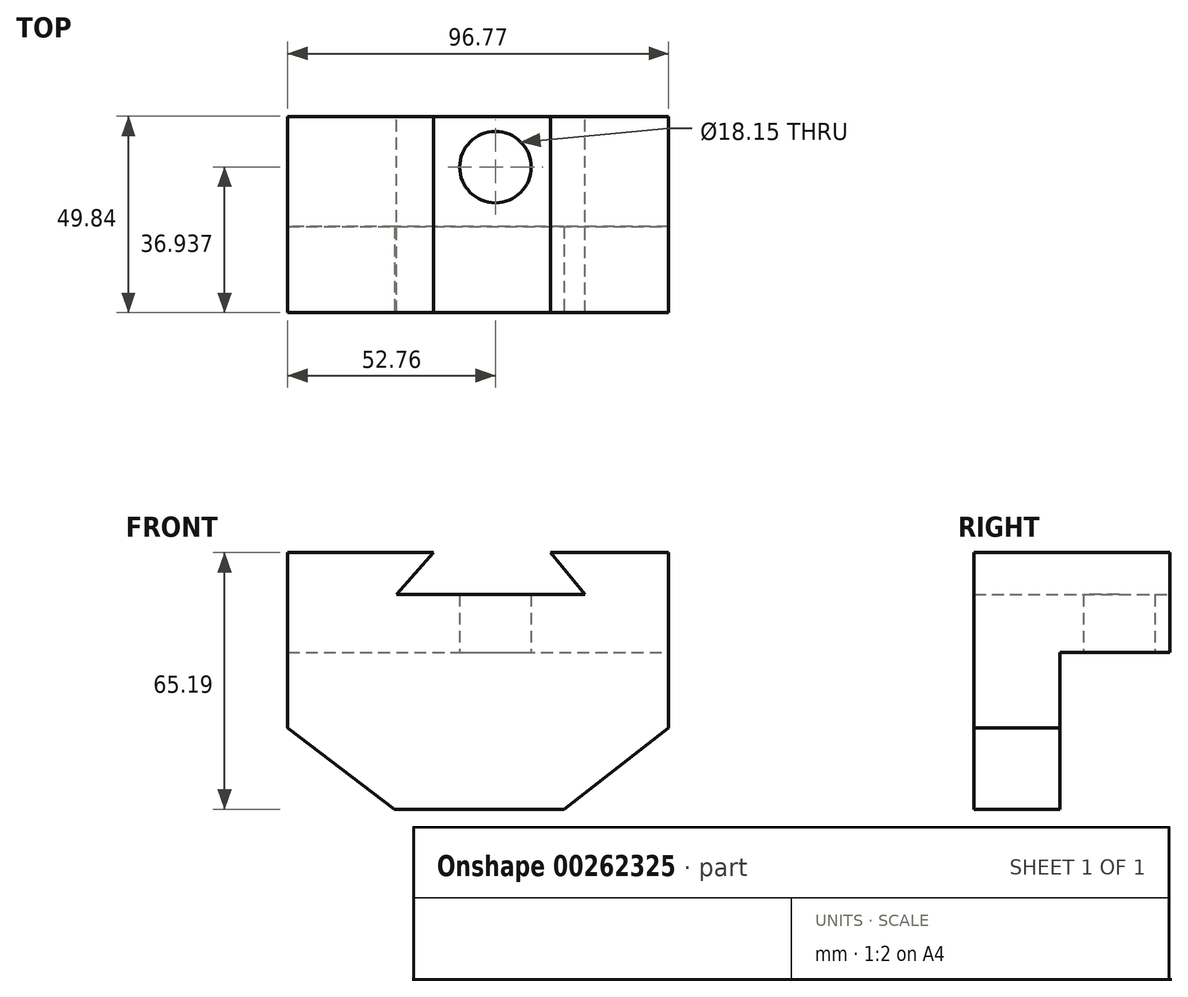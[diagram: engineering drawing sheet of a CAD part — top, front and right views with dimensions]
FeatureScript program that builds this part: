
annotation { "Feature Type Name" : "Feature", "Feature Type Description" : "" }
export const myFeature = defineFeature(function(context is Context, id is Id, definition is map)
    precondition{}
    {
        {
            var Q0;
            Q0=qCreatedBy(makeId("Top.planeOp"),FACE);
            var sketch = newSketch(context, id + "F0", { "sketchPlane" : qUnion([Q0])});
            skLineSegment(sketch, "E0.bottom", {"start": v(-52.76, 22.59) * mm, "end": v(44.01, 22.59) * mm});
            skLineSegment(sketch, "E0.top", {"start": v(-52.76, -27.25) * mm, "end": v(44.01, -27.25) * mm});
            skLineSegment(sketch, "E0.left", {"start": v(-52.76, 22.59) * mm, "end": v(-52.76, -27.25) * mm});
            skLineSegment(sketch, "E0.right", {"start": v(44.01, 22.59) * mm, "end": v(44.01, -27.25) * mm});
            skSolve(sketch);
        }
        {
            var Q0;
            Q0 = qSketchRegion(id + "F0", true);
            extrude(context, id + "F1", {"entities" : qUnion([Q0]), "depth" : 25.4 * mm});
        }
        {
            var Q0;
            Q0=makeQuery(id+"F1.opExtrude","SWEPT_FACE",FACE,{"disambiguationData":[OSD([sQuery(id+"F0.wireOp",EDGE,"E0.top")])]});
            var sketch = newSketch(context, id + "F2", { "sketchPlane" : qUnion([Q0])});
            skLineSegment(sketch, "E1.bottom", {"start": v(44.01, 25.4) * mm, "end": v(-52.76, 25.4) * mm});
            skLineSegment(sketch, "E1.top", {"start": v(44.01, -19.1) * mm, "end": v(-52.76, -19.1) * mm});
            skLineSegment(sketch, "E1.left", {"start": v(44.01, 25.4) * mm, "end": v(44.01, -19.1) * mm});
            skLineSegment(sketch, "E1.right", {"start": v(-52.76, 25.4) * mm, "end": v(-52.76, -19.1) * mm});
            skLineSegment(sketch, "E2", {"start": v(44.01, -19.1) * mm, "end": v(17.49, -39.79) * mm});
            skLineSegment(sketch, "E3", {"start": v(17.49, -39.79) * mm, "end": v(-25.65, -39.79) * mm});
            skLineSegment(sketch, "E4", {"start": v(-25.65, -39.79) * mm, "end": v(-52.76, -19.1) * mm});
            skSolve(sketch);
        }
        {
            var Q0;
            Q0 = qSketchRegion(id + "F2", true);
            extrude(context, id + "F3", {"entities" : qUnion([Q0]), "operationType" : NewBodyOperationType.ADD, "oppositeDirection" : true, "depth" : 21.84 * mm});
        }
        {
            var Q0;
            Q0=makeQuery(id+"F1.opExtrude","SWEPT_FACE",FACE,{"disambiguationData":[OSD([sQuery(id+"F0.wireOp",EDGE,"E0.bottom")])]});
            var sketch = newSketch(context, id + "F4", { "sketchPlane" : qUnion([Q0])});
            skLineSegment(sketch, "E5", {"start": v(15.74, 25.4) * mm, "end": v(25.07, 14.72) * mm});
            skLineSegment(sketch, "E6", {"start": v(25.07, 14.72) * mm, "end": v(-22.74, 14.72) * mm});
            skLineSegment(sketch, "E7", {"start": v(-22.74, 14.72) * mm, "end": v(-14, 25.4) * mm});
            skLineSegment(sketch, "E8", {"start": v(-14, 25.4) * mm, "end": v(15.74, 25.4) * mm});
            skSolve(sketch);
        }
        {
            var Q0;
            Q0 = qSketchRegion(id + "F4", true);
            extrude(context, id + "F5", {"entities" : qUnion([Q0]), "operationType" : NewBodyOperationType.REMOVE, "oppositeDirection" : true, "depth" : 64.52 * mm});
        }
        {
            var Q0;
            Q0=makeQuery(id+"F1.opExtrude","CAP_FACE",FACE,{"disambiguationData":[OSD([sQuery(id+"F0.wireOp",EDGE,"E0.bottom"),sQuery(id+"F0.wireOp",EDGE,"E0.top"),sQuery(id+"F0.wireOp",EDGE,"E0.left"),sQuery(id+"F0.wireOp",EDGE,"E0.right")])],"isStart":true});
            var sketch = newSketch(context, id + "F6", { "sketchPlane" : qUnion([Q0])});
            skCircle(sketch, "E9", {"center": v(0, -9.69) * mm, "radius": 9.07 * mm});
            skSolve(sketch);
        }
        {
            var Q0;
            Q0 = qSketchRegion(id + "F6", true);
            extrude(context, id + "F7", {"entities" : qUnion([Q0]), "operationType" : NewBodyOperationType.REMOVE, "oppositeDirection" : true, "depth" : 25.4 * mm});
        }
    });
